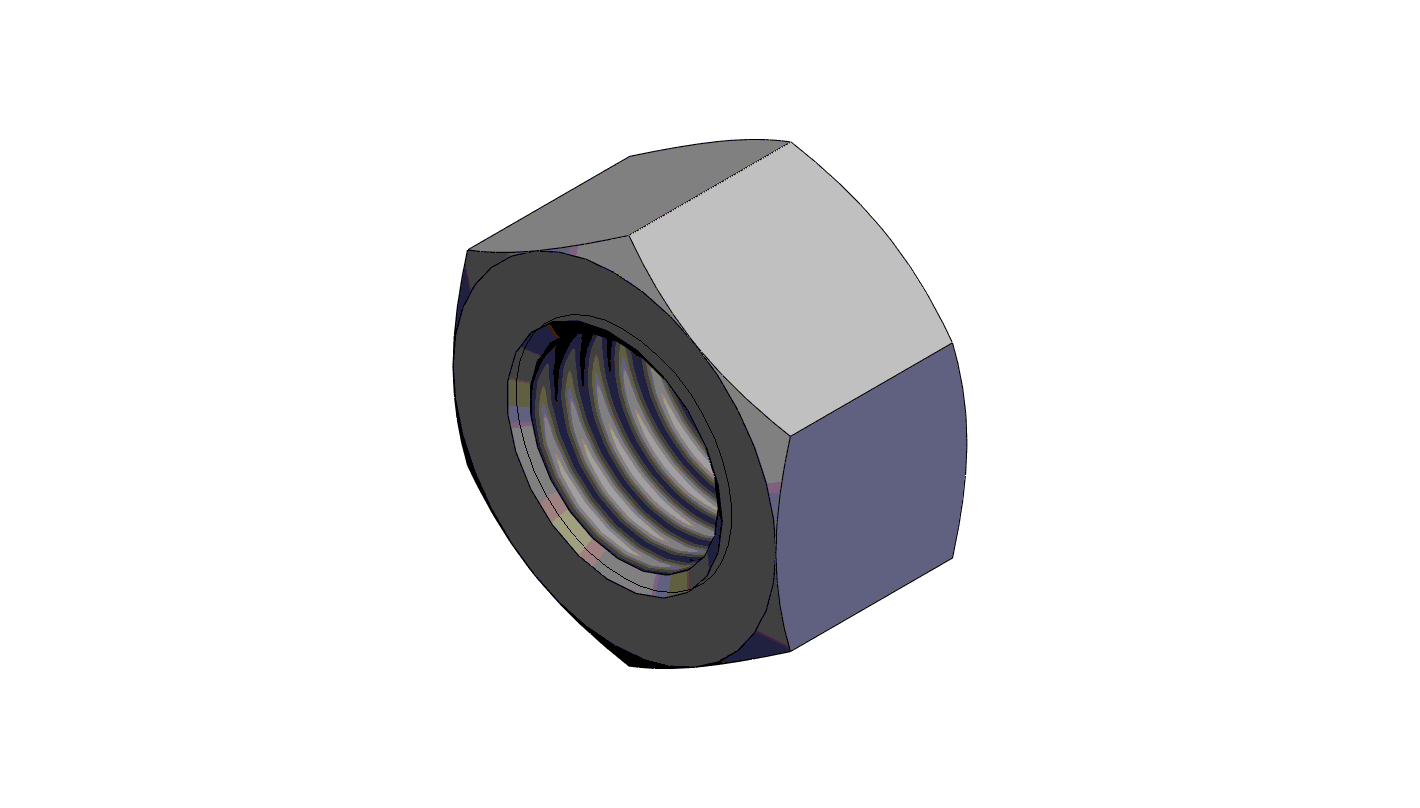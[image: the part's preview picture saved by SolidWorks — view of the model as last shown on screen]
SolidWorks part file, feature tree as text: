
SOLIDWORKS PART (.sldprt)
format: sldprt  version: not decoded by parser v0  size: 691,712 bytes
history: native  units: mm
features: sketch x5, cut_revolve x4, plane x3, material x1, extrude x1, thread x1, pattern_linear x1 (+9 scaffold rows collapsed)
feature tree (25):
  scaffold x9  (default folders/planes/origin — collapsed)
  material  "Material <nicht festgelegt>"
  plane  "Plane1"
  plane  "Plane2"
  plane  "Plane3"
  sketch  "BaseNutSke"  dims[c1.Tap_drill=3.3mm c1.D1=50.8mm c2.D1=30.0deg c2.D2=~24.797543mm c3.D2=60.0deg c3.D3=50.8mm c4.D3=30.0deg c4.D4=~24.797543mm c5.D4=60.0deg c6.D4=~24.797543mm c7.D4=60.0deg c8.D4=~24.797543mm c9.D4=60.0deg c9.Width_flats=7.0mm c9.D1=~21.475302mm c9.D2=~21.475302mm c10.D1=~21.475302mm c10.D2=3.5mm c10.D3=3.5mm c11.D1=~24.797543mm c12.D1=120.0deg c13.D1=~23.397294mm c14.D1=120.0deg c14.D4=3.5mm]
  extrude  "BaseNut"  [1 undecoded]
  thread  "ThreadCosmetic"  Diameter=4mm Thread_major=4mm  [1 undecoded]
  cut_revolve  "EndChamfer"  [1 undecoded]
  sketch  "Sketch5"
  pattern_linear  "ThdSchPat"  [2 undecoded]
  cut_revolve  "ThreadSchematic"  [1 undecoded]
  sketch  "ThdSchSke"  dims[c1.D1=~4.490128mm c2.D1=90.0deg c3.D1=~4.490128mm c3.VeeAngle=70.0deg c4.D1=19.5834mm c4.SideAngle=55.0deg c5.D1=~4.490128mm c5.SideAngle=55.0deg c5.ThreadDepth=2.54mm c6.ThreadDepth=3.175mm c6.Thread_Major=6.35mm c6.D1=~9.573347mm c6.D2=~9.428305mm c6.OverCut=1.65mm c6.Tap_Drill=3.3mm c6.Advance=1.27mm c6.Thread_major=4.0mm c7.Advance=0.7mm c7.D1=6.35mm c7.D2=0.0254mm c8.D1=0.0254mm c9.D1=360.0deg c9.Num_threads=6.0 c9.Advance=~0.62984mm c9.D2=1.0 c9.D4=50.0mm c10.D1=~8.980256mm c11.D1=315.0deg c12.D1=~8.980256mm c13.D1=45.0deg c13.D2=~8.94581mm c14.D2=~1.952549deg c14.D3=6.35mm c15.D2=25.7048mm c15.D1=~6.352235mm c16.D1=35.0deg c16.D2=12.7mm c16.D3=12.7mm c17.D2=22.5552mm c17.D3=25.4mm c17.D4=12.7mm c18.D3=12.7mm c18.D2=0.0508mm c18.Offset1=25.4254mm c18.ThreadMajor=12.7mm c18.ChamferDepth=0.385mm c18.Offset2=3.2762mm c19.ThreadMajor=2.0mm c19.Offset1=3.2254mm c19.D1=360.0deg c19.Thickness=3.2mm]
  sketch  "Sketch4"  dims[c1.D1=38.1mm c1.Bearing_ht=0.4mm c1.D3=12.7mm c1.D4=10.0mm c1.D5=2.54mm c1.D6=18.8722mm c2.D3=10.0mm c2.D1=3.5mm c2.D2=~3.890588mm c3.D2=~139.242599deg c4.D2=22.5298mm c5.D2=45.0deg c6.D2=~10.392305mm c7.D2=30.0deg]
  cut_revolve  "Bearing-Face"  Angle=360deg
  sketch  "Sketch3"  dims[c1.D1=3.5mm c1.D2=2.4mm c1.D3=12.7mm c1.D4=10.0mm c1.D5=10.9093mm c1.D6=~10.998523mm c2.D6=~179.413404deg c3.D6=~2.539714mm c3.D3=10.0mm c3.D5=9.525mm c3.D2=~10.392305mm c4.D2=30.0deg]
  cut_revolve  "Double-Chamfer"  Angle=360deg
decode coverage: 7 of 12 modeling features carry decoded parameters
note: ~ marks probable driven/reference dimensions
note: 6 parameter values undecoded
summary: no parameter record found for 3 features
note: suppression state not decoded; provenance and decode notes live in map.json
